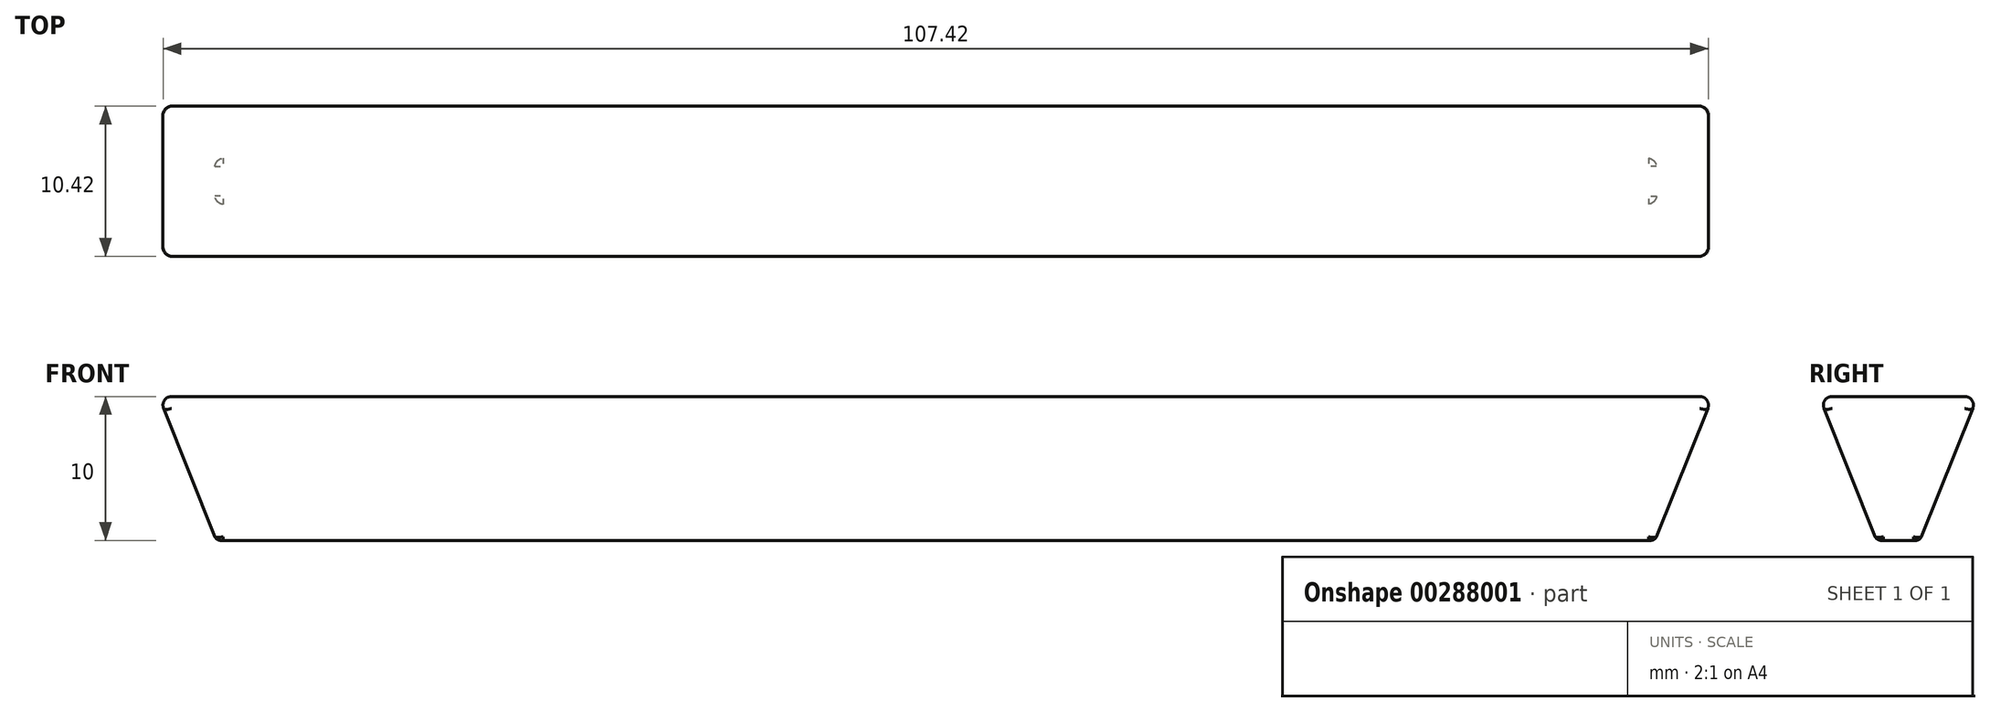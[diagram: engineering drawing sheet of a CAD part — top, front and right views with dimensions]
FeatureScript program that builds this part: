
annotation { "Feature Type Name" : "Feature", "Feature Type Description" : "" }
export const myFeature = defineFeature(function(context is Context, id is Id, definition is map)
    precondition{}
    {
        {
            var Q0;
            Q0=qCreatedBy(makeId("Top.planeOp"),FACE);
            var sketch = newSketch(context, id + "F0", { "sketchPlane" : qUnion([Q0])});
            skLineSegment(sketch, "E0.bottom", {"start": v(-50, 1.5) * mm, "end": v(50, 1.5) * mm});
            skLineSegment(sketch, "E0.top", {"start": v(-50, -1.5) * mm, "end": v(50, -1.5) * mm});
            skLineSegment(sketch, "E0.left", {"start": v(-50, 1.5) * mm, "end": v(-50, -1.5) * mm});
            skLineSegment(sketch, "E0.right", {"start": v(50, 1.5) * mm, "end": v(50, -1.5) * mm});
            skPoint(sketch, "E0.middle", {"position": v(0, 0) * mm});
            skSolve(sketch);
        }
        {
            var Q0;
            Q0=qCreatedBy(makeId("Top.planeOp"),FACE);
            cPlane(context, id + "F1", {"entities" : qUnion([Q0]), "cplaneType" : CPlaneType.OFFSET, "offset" : 10 * mm, "width" : 150 * mm, "height" : 150 * mm});
        }
        {
            var Q0;
            Q0=qCreatedBy(id+"F1.planeOp",FACE);
            var sketch = newSketch(context, id + "F2", { "sketchPlane" : qUnion([Q0])});
            skLineSegment(sketch, "E1.bottom", {"start": v(-54, 5.5) * mm, "end": v(54, 5.5) * mm});
            skLineSegment(sketch, "E1.top", {"start": v(-54, -5.5) * mm, "end": v(54, -5.5) * mm});
            skLineSegment(sketch, "E1.left", {"start": v(-54, 5.5) * mm, "end": v(-54, -5.5) * mm});
            skLineSegment(sketch, "E1.right", {"start": v(54, 5.5) * mm, "end": v(54, -5.5) * mm});
            skPoint(sketch, "E1.middle", {"position": v(0, 0) * mm});
            skSolve(sketch);
        }
        {
            var Q0;
            Q0=makeQuery(id+"F0.imprint","IMPRINT",FACE,{"disambiguationData":[TD([[makeQuery(id+"F0.imprint","IMPRINT",EDGE,{"derivedFrom":sQuery(id+"F0.wireOp",EDGE,"E0.bottom")}),-1.0]])]});
            var Q1;
            Q1=makeQuery(id+"F2.imprint","IMPRINT",FACE,{"disambiguationData":[TD([[makeQuery(id+"F2.imprint","IMPRINT",EDGE,{"derivedFrom":sQuery(id+"F2.wireOp",EDGE,"E1.bottom")}),-1.0]])]});
            loft(context, id + "F3", {"sheetProfilesArray" : [{ "sheetProfileEntities" : qUnion([Q0]) }, { "sheetProfileEntities" : qUnion([Q1]) }]});
        }
        {
            var Q0;
            Q0=makeQuery(id+"F3.opLoft","CAP_FACE",FACE,{"disambiguationData":[OSD([makeQuery(id+"F2.imprint","IMPRINT",FACE,{"disambiguationData":[TD([[makeQuery(id+"F2.imprint","IMPRINT",EDGE,{"derivedFrom":sQuery(id+"F2.wireOp",EDGE,"E1.bottom")}),-1.0]])]})])],"isStart":true});
            var Q1;
            Q1=makeQuery(id+"F3.opLoft","SWEPT_EDGE",EDGE,{"disambiguationData":[OSD([sQuery(id+"F0.wireOp",EDGE,"E0.top"),sQuery(id+"F0.wireOp",EDGE,"E0.right"),sQuery(id+"F2.wireOp",EDGE,"E1.top"),sQuery(id+"F2.wireOp",EDGE,"E1.right")])]});
            var Q2;
            Q2=makeQuery(id+"F3.opLoft","SWEPT_EDGE",EDGE,{"disambiguationData":[OSD([sQuery(id+"F0.wireOp",EDGE,"E0.bottom"),sQuery(id+"F0.wireOp",EDGE,"E0.right"),sQuery(id+"F2.wireOp",EDGE,"E1.bottom"),sQuery(id+"F2.wireOp",EDGE,"E1.right")])]});
            var Q3;
            Q3=makeQuery(id+"F3.opLoft","SWEPT_EDGE",EDGE,{"disambiguationData":[OSD([sQuery(id+"F0.wireOp",EDGE,"E0.top"),sQuery(id+"F0.wireOp",EDGE,"E0.left"),sQuery(id+"F2.wireOp",EDGE,"E1.top"),sQuery(id+"F2.wireOp",EDGE,"E1.left")])]});
            var Q4;
            Q4=makeQuery(id+"F3.opLoft","SWEPT_EDGE",EDGE,{"disambiguationData":[OSD([sQuery(id+"F0.wireOp",EDGE,"E0.bottom"),sQuery(id+"F0.wireOp",EDGE,"E0.left"),sQuery(id+"F2.wireOp",EDGE,"E1.bottom"),sQuery(id+"F2.wireOp",EDGE,"E1.left")])]});
            fillet(context, id + "F4", {"entities" : qUnion([Q0, Q1, Q2, Q3, Q4]), "radius" : 0.6 * mm, "tangentPropagation" : true, "allowEdgeOverflow" : false});
        }
        {
            var Q0;
            Q0=makeQuery(id+"F3.opLoft","CAP_FACE",FACE,{"disambiguationData":[OSD([makeQuery(id+"F0.imprint","IMPRINT",FACE,{"disambiguationData":[TD([[makeQuery(id+"F0.imprint","IMPRINT",EDGE,{"derivedFrom":sQuery(id+"F0.wireOp",EDGE,"E0.bottom")}),-1.0]])]})])],"isStart":true});
            fillet(context, id + "F5", {"entities" : qUnion([Q0]), "radius" : 0.4 * mm, "tangentPropagation" : true, "allowEdgeOverflow" : false});
        }
    });
